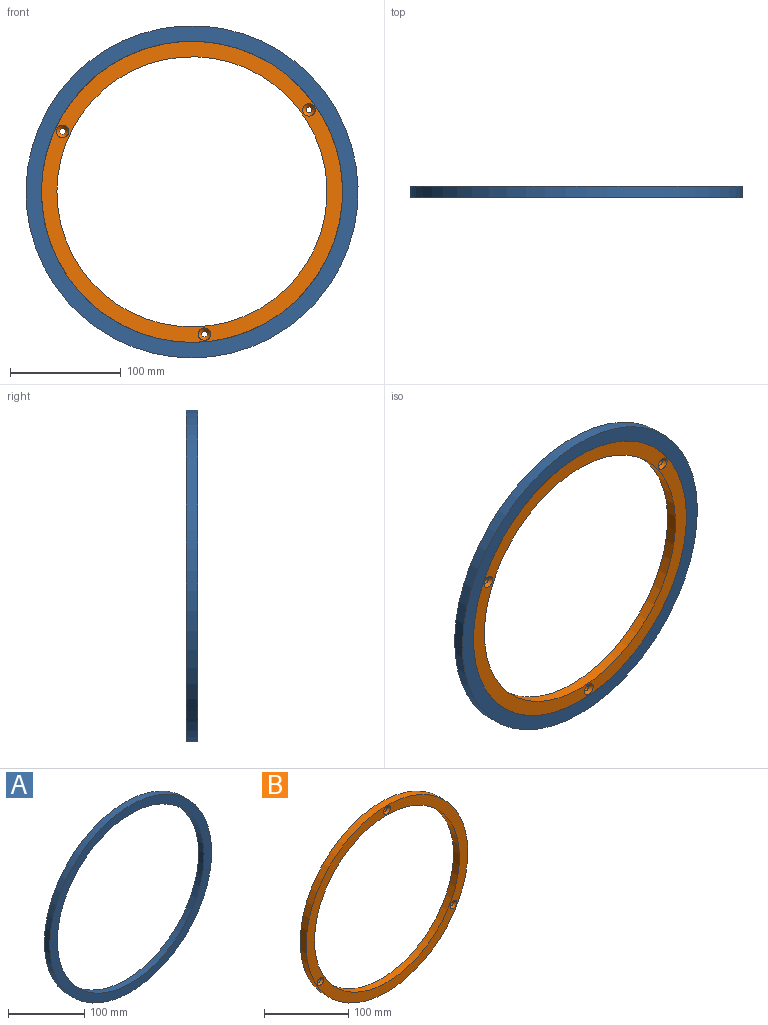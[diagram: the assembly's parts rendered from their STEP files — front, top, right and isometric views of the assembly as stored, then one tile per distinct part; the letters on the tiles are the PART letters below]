
ASSEMBLY  parts=2 mates=1
PART A: 4 faces, bbox 300x10x300 mm
  f0: cylinder r=136mm len=272mm, axis (0,1,0), area 8545.1mm2, adj f2,f3
  f1: cylinder r=150mm len=300mm, axis (0,1,0), area 9424.8mm2, adj f2,f3
  f2: plane 300x300mm, normal (0,-1,0), area 12578.9mm2, adj f0,f1
  f3: plane 300x300mm, normal (0,1,0), area 12578.9mm2, adj f0,f1
PART B: 10 faces, bbox 272x10x272 mm
  f0: cylinder r=122mm len=244mm, axis (0,1,0), area 7665.5mm2, adj f2,f3
  f1: cylinder r=136mm len=272mm, axis (0,1,0), area 8545.1mm2, adj f2,f3
  f2: plane 272x272mm, normal (0,-1,0), area 11051.9mm2, adj f0,f1,f5,f7,f9
  f3: plane 272x272mm, normal (0,1,0), area 11276.2mm2, adj f0,f1,f4,f6,f8
  f4: cylinder r=2.75mm len=7.15mm, axis (0,-1,0), area 123.5mm2, adj f3,f5
  f5: cone r=2.75mm half-angle=45deg, axis (0,-1,0), area 105.7mm2, adj f2,f4
  f6: cylinder r=2.75mm len=7.15mm, axis (0,-1,0), area 123.5mm2, adj f3,f7
  f7: cone r=2.75mm half-angle=45deg, axis (0,-1,0), area 105.7mm2, adj f2,f6
  f8: cylinder r=2.75mm len=7.15mm, axis (0,-1,0), area 123.5mm2, adj f3,f9
  f9: cone r=2.75mm half-angle=45deg, axis (0,-1,0), area 105.7mm2, adj f2,f8
PLACE A t=(-147.98,-60.44,-4.74)mm fixed
PLACE B rot(axis=(0,1,0),55deg) t=(-222.35,-60.44,-90.23)mm
MATE revolute B.f0 <-> A.f0  axis (0,-1,0) through (-267.27,-70.44,23.95)mm
